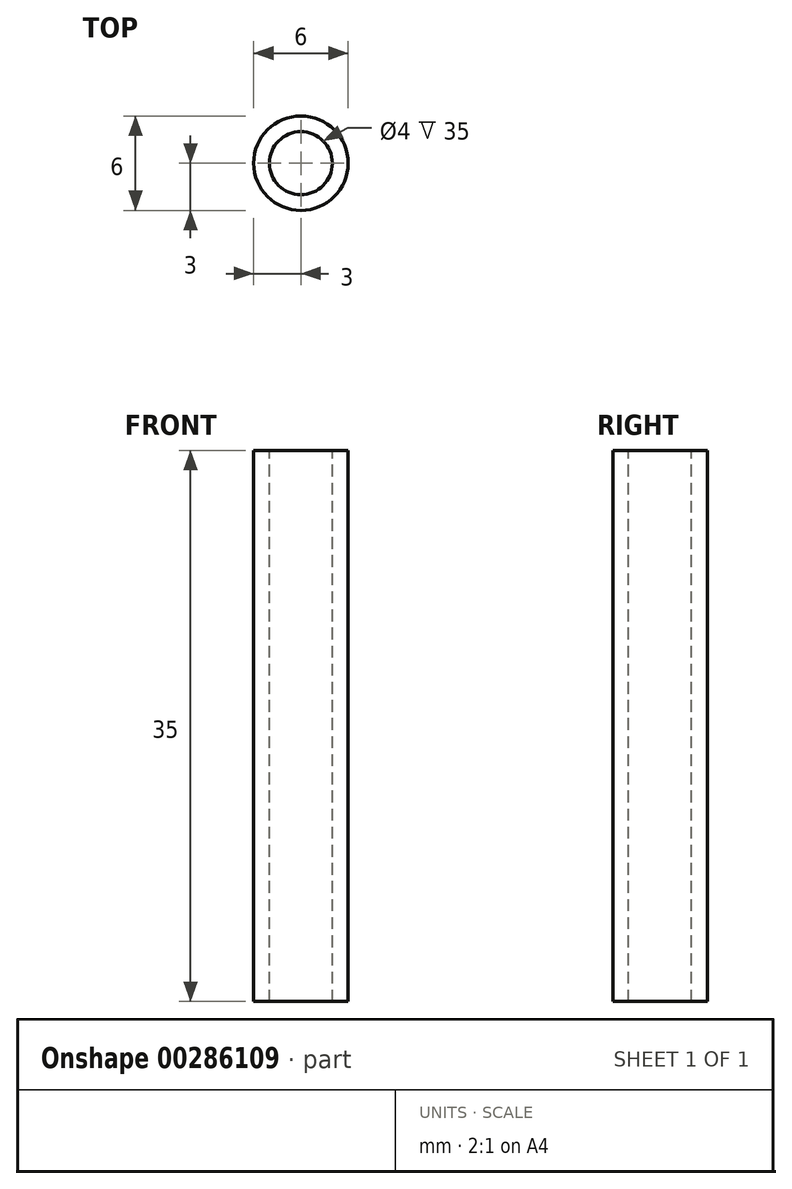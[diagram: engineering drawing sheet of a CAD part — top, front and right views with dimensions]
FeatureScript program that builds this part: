
annotation { "Feature Type Name" : "Feature", "Feature Type Description" : "" }
export const myFeature = defineFeature(function(context is Context, id is Id, definition is map)
    precondition{}
    {
        {
            var Q0;
            Q0=qCreatedBy(makeId("Top.planeOp"),FACE);
            var sketch = newSketch(context, id + "F0", { "sketchPlane" : qUnion([Q0])});
            skCircle(sketch, "E0", {"center": v(0, 0) * mm, "radius": 3 * mm});
            skSolve(sketch);
        }
        {
            var Q0;
            Q0=makeQuery(id+"F0.imprint","IMPRINT",FACE,{"disambiguationData":[TD([[makeQuery(id+"F0.imprint","IMPRINT",EDGE,{"derivedFrom":sQuery(id+"F0.wireOp",EDGE,"E0")}),1.0]])]});
            extrude(context, id + "F1", {"entities" : qUnion([Q0]), "depth" : 35 * mm});
        }
        {
            var Q0;
            Q0=makeQuery(id+"F1.opExtrude","CAP_FACE",FACE,{"disambiguationData":[OSD([sQuery(id+"F0.wireOp",EDGE,"E0")])],"isStart":false});
            var sketch = newSketch(context, id + "F2", { "sketchPlane" : qUnion([Q0])});
            skCircle(sketch, "E1", {"center": v(0, 0) * mm, "radius": 2 * mm});
            skSolve(sketch);
        }
        {
            var Q0;
            Q0=qSketchRegion(id+"F2",true);
            extrude(context, id + "F3", {"entities" : qUnion([Q0]), "operationType" : NewBodyOperationType.REMOVE, "endBound" : BoundingType.THROUGH_ALL, "oppositeDirection" : true, "depth" : 25 * mm});
        }
    });
